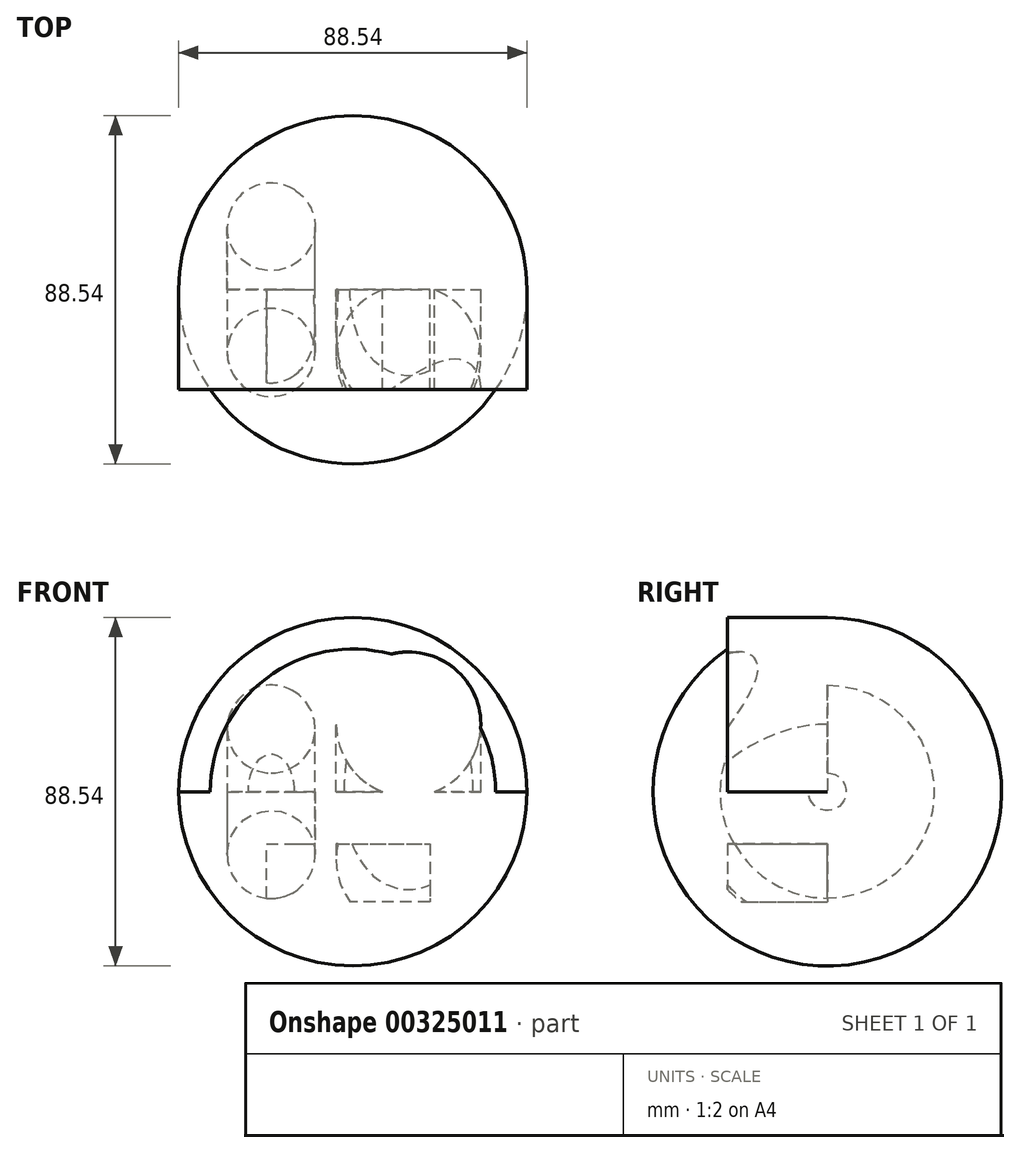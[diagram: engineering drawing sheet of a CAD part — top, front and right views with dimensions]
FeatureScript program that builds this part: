
annotation { "Feature Type Name" : "Feature", "Feature Type Description" : "" }
export const myFeature = defineFeature(function(context is Context, id is Id, definition is map)
    precondition{}
    {
        {
            var Q0;
            Q0=qCreatedBy(makeId("Front.planeOp"),FACE);
            var sketch = newSketch(context, id + "F0", { "sketchPlane" : qUnion([Q0])});
            skCircle(sketch, "E0", {"center": v(0, 0) * mm, "radius": 44.27 * mm});
            skLineSegment(sketch, "E1", {"start": v(-44.27, 0) * mm, "end": v(44.27, 0) * mm});
            skCircle(sketch, "E2", {"center": v(-20.75, 15.94) * mm, "radius": 11.17 * mm});
            skCircle(sketch, "E3", {"center": v(14.14, 17.15) * mm, "radius": 18.37 * mm});
            skLineSegment(sketch, "E4", {"start": v(-21.96, -13.23) * mm, "end": v(19.55, -13.23) * mm});
            skLineSegment(sketch, "E5", {"start": v(19.55, -13.23) * mm, "end": v(19.55, -27.97) * mm});
            skLineSegment(sketch, "E6", {"start": v(19.55, -27.97) * mm, "end": v(-21.96, -27.97) * mm});
            skLineSegment(sketch, "E7", {"start": v(-21.96, -27.97) * mm, "end": v(-21.96, -13.23) * mm});
            skSolve(sketch);
        }
        {
            var Q0;
            {var subQ0=sQuery(id+"F0.wireOp",EDGE,"E1");Q0=makeQuery(id+"F0.imprint","IMPRINT",FACE,{"disambiguationData":[TD([[makeQuery(id+"F0.imprint","IMPRINT",EDGE,{"derivedFrom":subQ0}),1.0]])]});}
            var Q1;
            Q1=sQuery(id+"F0.wireOp",EDGE,"E1");
            revolve(context, id + "F1", {"entities" : qUnion([Q0]), "axis" : qUnion([Q1]), "revolveType" : RevolveType.FULL});
        }
        {
            var Q0;
            Q0=makeQuery(id+"F0.imprint","IMPRINT",FACE,{"disambiguationData":[TD([[makeQuery(id+"F0.imprint","IMPRINT",EDGE,{"derivedFrom":sQuery(id+"F0.wireOp",EDGE,"E4")}),-1.0]])]});
            var Q1;
            Q1=makeQuery(id+"F0.imprint","IMPRINT",FACE,{"disambiguationData":[TD([[makeQuery(id+"F0.imprint","IMPRINT",EDGE,{"derivedFrom":sQuery(id+"F0.wireOp",EDGE,"E2")}),1.0]])]});
            var Q2;
            {var subQ0=sQuery(id+"F0.wireOp",EDGE,"E3");var subQ1=sQuery(id+"F0.wireOp",EDGE,"E1");var subQ2=makeQuery(id+"F0.imprint","INTERSECT",VERTEX,{"disambiguationData":[OD(0.0)],"derivedFrom":[subQ1,subQ0]});Q2=makeQuery(id+"F0.imprint","IMPRINT",FACE,{"disambiguationData":[TD([[makeQuery(id+"F0.imprint","IMPRINT",EDGE,{"disambiguationData":[TD([[subQ2,-1.0]])],"derivedFrom":subQ1}),1.0]])]});}
            extrude(context, id + "F2", {"entities" : qUnion([Q0, Q1, Q2]), "operationType" : NewBodyOperationType.ADD, "depth" : 25.4 * mm});
        }
    });
